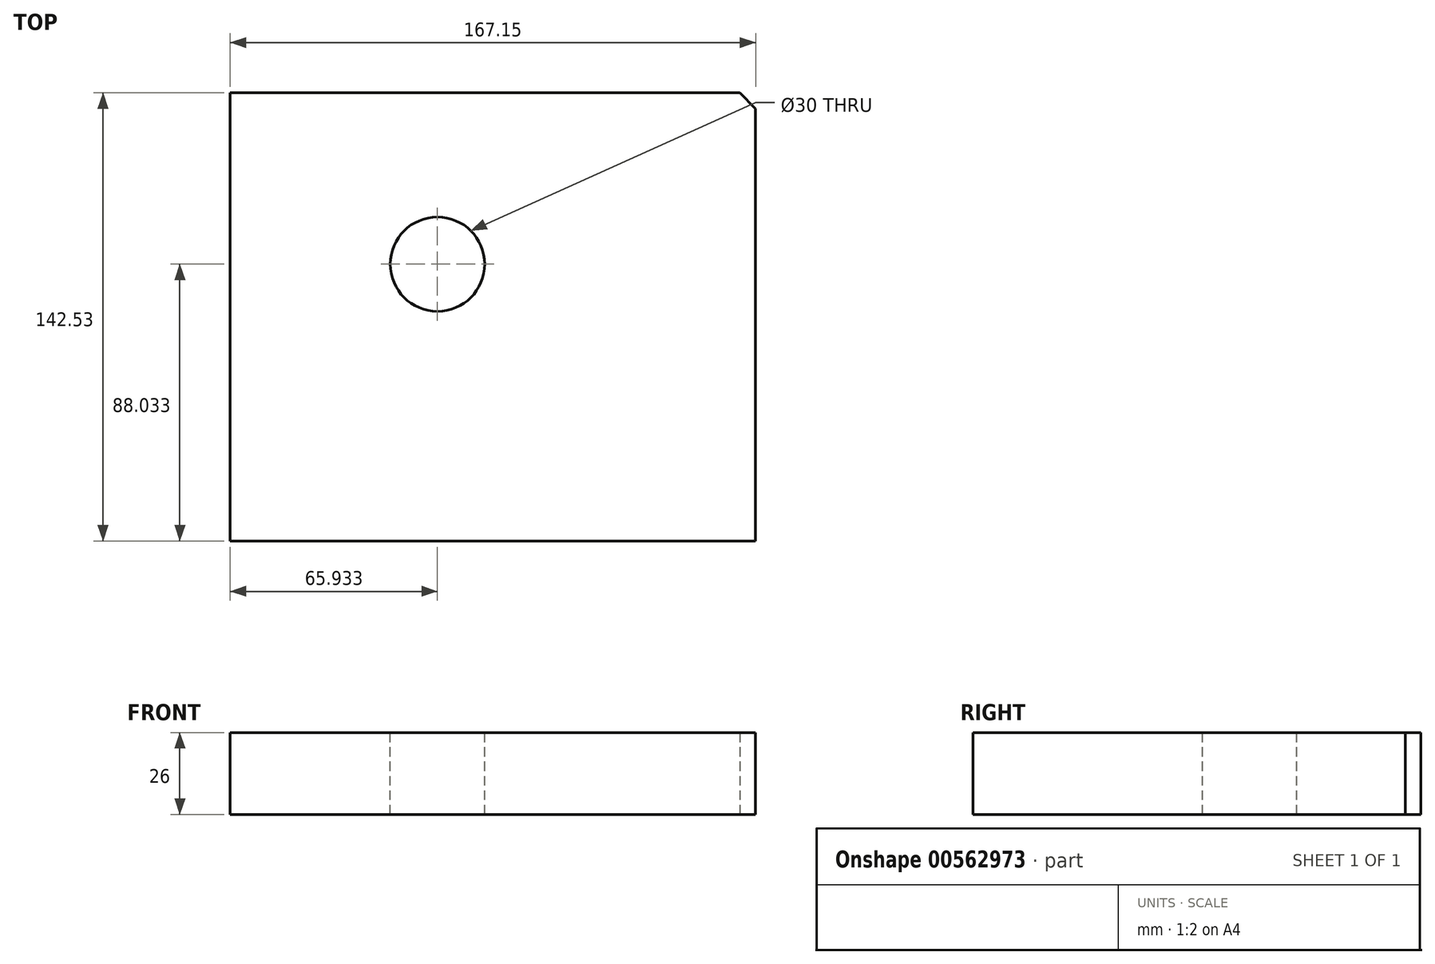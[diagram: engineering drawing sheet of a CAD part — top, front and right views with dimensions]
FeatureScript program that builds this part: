
annotation { "Feature Type Name" : "Feature", "Feature Type Description" : "" }
export const myFeature = defineFeature(function(context is Context, id is Id, definition is map)
    precondition{}
    {
        {
            var Q0;
            Q0=qCreatedBy(makeId("Top.planeOp"),FACE);
            var sketch = newSketch(context, id + "F0", { "sketchPlane" : qUnion([Q0])});
            skLineSegment(sketch, "E0.bottom", {"start": v(-111.23, 25.67) * mm, "end": v(55.92, 25.67) * mm});
            skLineSegment(sketch, "E0.top", {"start": v(-111.23, -116.86) * mm, "end": v(55.92, -116.86) * mm});
            skLineSegment(sketch, "E0.left", {"start": v(-111.23, 25.67) * mm, "end": v(-111.23, -116.86) * mm});
            skLineSegment(sketch, "E0.right", {"start": v(55.92, 25.67) * mm, "end": v(55.92, -116.86) * mm});
            skSolve(sketch);
        }
        {
            var Q0;
            Q0 = qSketchRegion(id + "F0", true);
            extrude(context, id + "F1", {"entities" : qUnion([Q0]), "depth" : 26 * mm, "offsetDistance" : 25 * mm});
        }
        {
            var Q0;
            Q0=makeQuery(id+"F1.opExtrude","SWEPT_EDGE",EDGE,{"disambiguationData":[OSD([sQuery(id+"F0.wireOp",EDGE,"E0.bottom"),sQuery(id+"F0.wireOp",EDGE,"E0.right")])]});
            chamfer(context, id + "F2", {"entities" : qUnion([Q0]), "width" : 5 * mm, "tangentPropagation" : true});
        }
        {
            var Q0;
            Q0=makeQuery(id+"F1.opExtrude","CAP_FACE",FACE,{"disambiguationData":[OSD([sQuery(id+"F0.wireOp",EDGE,"E0.bottom"),sQuery(id+"F0.wireOp",EDGE,"E0.top"),sQuery(id+"F0.wireOp",EDGE,"E0.left"),sQuery(id+"F0.wireOp",EDGE,"E0.right")])],"isStart":false});
            var sketch = newSketch(context, id + "F3", { "sketchPlane" : qUnion([Q0])});
            skCircle(sketch, "E1", {"center": v(-45.3, -28.83) * mm, "radius": 15 * mm});
            skSolve(sketch);
        }
        {
            var Q0;
            Q0 = qSketchRegion(id + "F3", true);
            extrude(context, id + "F4", {"entities" : qUnion([Q0]), "operationType" : NewBodyOperationType.REMOVE, "oppositeDirection" : true, "depth" : 889 * mm, "offsetDistance" : 25 * mm});
        }
    });
